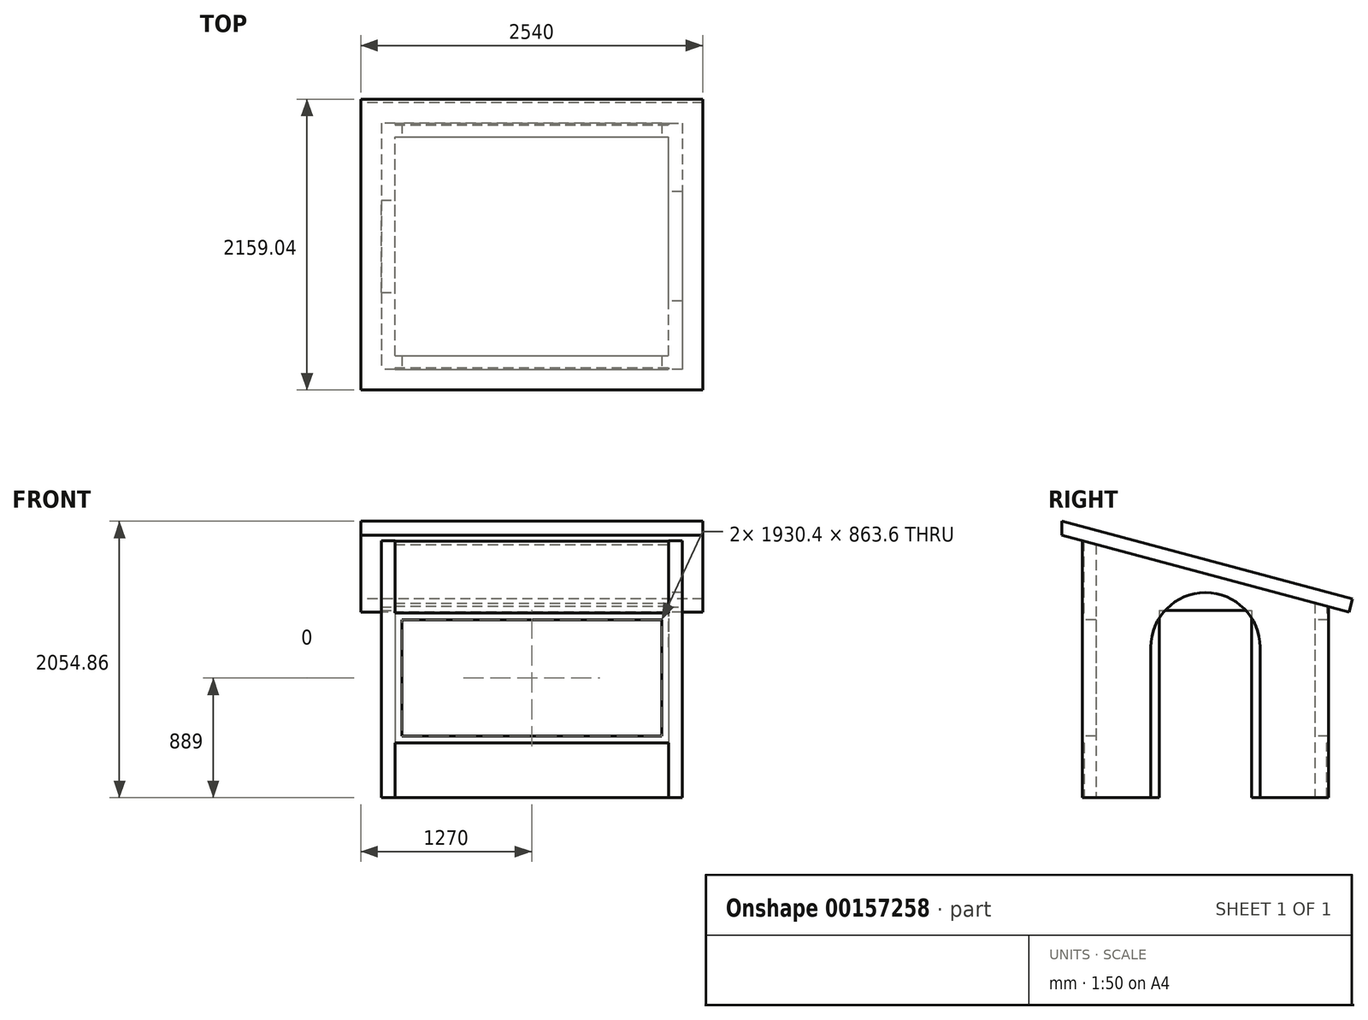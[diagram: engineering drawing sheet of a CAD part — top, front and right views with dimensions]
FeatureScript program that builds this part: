
annotation { "Feature Type Name" : "Feature", "Feature Type Description" : "" }
export const myFeature = defineFeature(function(context is Context, id is Id, definition is map)
    precondition{}
    {
        {
            var Q0;
            Q0=qCreatedBy(makeId("Right.planeOp"),FACE);
            var sketch = newSketch(context, id + "F0", { "sketchPlane" : qUnion([Q0])});
            skLineSegment(sketch, "E0", {"start": v(-914.4, 0) * mm, "end": v(-914.4, 2014.03) * mm});
            skLineSegment(sketch, "E1", {"start": v(-914.4, 2014.03) * mm, "end": v(914.4, 1524) * mm});
            skLineSegment(sketch, "E2", {"start": v(914.4, 1524) * mm, "end": v(914.4, 0) * mm});
            skLineSegment(sketch, "E3", {"start": v(914.4, 0) * mm, "end": v(-914.4, 0) * mm});
            skLineSegment(sketch, "E4", {"start": v(914.4, 1524) * mm, "end": v(-914.4, 1524) * mm, "construction": true});
            skLineSegment(sketch, "E5", {"start": v(0, 1524) * mm, "end": v(0, 0) * mm, "construction": true});
            skSolve(sketch);
        }
        {
            var Q0;
            Q0=makeQuery(id+"F0.imprint","IMPRINT",FACE,{"disambiguationData":[TD([[makeQuery(id+"F0.imprint","IMPRINT",EDGE,{"derivedFrom":sQuery(id+"F0.wireOp",EDGE,"E0")}),-1.0]])]});
            extrude(context, id + "F1", {"entities" : qUnion([Q0]), "endBound" : BoundingType.SYMMETRIC, "depth" : 2235.2 * mm});
        }
        {
            var Q0;
            Q0=qCreatedBy(makeId("Front.planeOp"),FACE);
            var sketch = newSketch(context, id + "F2", { "sketchPlane" : qUnion([Q0])});
            skLineSegment(sketch, "E6.bottom", {"start": v(-965.2, 1320.8) * mm, "end": v(965.2, 1320.8) * mm});
            skLineSegment(sketch, "E6.top", {"start": v(-965.2, 457.2) * mm, "end": v(965.2, 457.2) * mm});
            skLineSegment(sketch, "E6.left", {"start": v(-965.2, 1320.8) * mm, "end": v(-965.2, 457.2) * mm});
            skLineSegment(sketch, "E6.right", {"start": v(965.2, 1320.8) * mm, "end": v(965.2, 457.2) * mm});
            skLineSegment(sketch, "E7", {"start": v(0, 0) * mm, "end": v(0, 1954.27) * mm, "construction": true});
            skSolve(sketch);
        }
        {
            var Q0;
            Q0 = qSketchRegion(id + "F2", true);
            extrude(context, id + "F3", {"entities" : qUnion([Q0]), "operationType" : NewBodyOperationType.REMOVE, "endBound" : BoundingType.THROUGH_ALL, "oppositeDirection" : true, "depth" : 25.4 * mm, "hasSecondDirection" : true, "secondDirectionBound" : SecondDirectionBoundingType.THROUGH_ALL, "secondDirectionOppositeDirection" : false, "secondDirectionDepth" : 25.4 * mm});
        }
        {
            var Q0;
            Q0=qCreatedBy(makeId("Right.planeOp"),FACE);
            var sketch = newSketch(context, id + "F4", { "sketchPlane" : qUnion([Q0])});
            skLineSegment(sketch, "E8", {"start": v(0, 0) * mm, "end": v(0, 2189.15) * mm, "construction": true});
            skLineSegment(sketch, "E9.bottom", {"start": v(-342.9, 1390.65) * mm, "end": v(342.9, 1390.65) * mm});
            skLineSegment(sketch, "E9.top", {"start": v(-342.9, 0) * mm, "end": v(342.9, 0) * mm});
            skLineSegment(sketch, "E9.left", {"start": v(-342.9, 1390.65) * mm, "end": v(-342.9, 0) * mm});
            skLineSegment(sketch, "E9.right", {"start": v(342.9, 1390.65) * mm, "end": v(342.9, 0) * mm});
            skSolve(sketch);
        }
        {
            var Q0;
            Q0 = qSketchRegion(id + "F4", true);
            extrude(context, id + "F5", {"entities" : qUnion([Q0]), "operationType" : NewBodyOperationType.REMOVE, "endBound" : BoundingType.THROUGH_ALL, "oppositeDirection" : true, "depth" : 25.4 * mm});
        }
        {
            var Q0;
            Q0=qCreatedBy(makeId("Right.planeOp"),FACE);
            var sketch = newSketch(context, id + "F6", { "sketchPlane" : qUnion([Q0])});
            skLineSegment(sketch, "E10", {"start": v(-1066.8, 2054.86) * mm, "end": v(1092.24, 1476.35) * mm});
            skLineSegment(sketch, "E11", {"start": v(-1066.8, 2054.86) * mm, "end": v(-1066.8, 1949.68) * mm});
            skLineSegment(sketch, "E12", {"start": v(-1066.8, 1949.68) * mm, "end": v(1065.94, 1378.21) * mm});
            skLineSegment(sketch, "E13", {"start": v(1065.94, 1378.21) * mm, "end": v(1092.24, 1476.35) * mm});
            skSolve(sketch);
        }
        {
            var Q0;
            Q0=makeQuery(id+"F6.imprint","IMPRINT",FACE,{"disambiguationData":[TD([[makeQuery(id+"F6.imprint","IMPRINT",EDGE,{"derivedFrom":sQuery(id+"F6.wireOp",EDGE,"E10")}),-1.0]])]});
            extrude(context, id + "F7", {"entities" : qUnion([Q0]), "operationType" : NewBodyOperationType.ADD, "endBound" : BoundingType.SYMMETRIC, "depth" : 2540 * mm});
        }
        {
            var Q0;
            Q0=qCreatedBy(makeId("Top.planeOp"),FACE);
            var sketch = newSketch(context, id + "F8", { "sketchPlane" : qUnion([Q0])});
            skLineSegment(sketch, "E14", {"start": v(0, -730.46) * mm, "end": v(0, 588.36) * mm, "construction": true});
            skLineSegment(sketch, "E15", {"start": v(-1194.95, 0) * mm, "end": v(1199.4, 0) * mm, "construction": true});
            skLineSegment(sketch, "E16.bottom", {"start": v(-1016, -812.8) * mm, "end": v(1016, -812.8) * mm});
            skLineSegment(sketch, "E16.top", {"start": v(-1016, 812.8) * mm, "end": v(1016, 812.8) * mm});
            skLineSegment(sketch, "E16.left", {"start": v(-1016, -812.8) * mm, "end": v(-1016, 812.8) * mm});
            skLineSegment(sketch, "E16.right", {"start": v(1016, -812.8) * mm, "end": v(1016, 812.8) * mm});
            skSolve(sketch);
        }
        {
            var Q0;
            Q0 = qSketchRegion(id + "F8", true);
            var Q1;
            Q1=makeQuery(id+"F7.opExtrude","SWEPT_FACE",FACE,{"disambiguationData":[OSD([sQuery(id+"F6.wireOp",EDGE,"E12")])]});
            extrude(context, id + "F9", {"entities" : qUnion([Q0]), "operationType" : NewBodyOperationType.REMOVE, "endBound" : BoundingType.UP_TO_SURFACE, "endBoundEntityFace" : qUnion([Q1]), "depth" : 25.4 * mm});
        }
        {
            var Q0;
            Q0=qCreatedBy(makeId("Right.planeOp"),FACE);
            var sketch = newSketch(context, id + "F10", { "sketchPlane" : qUnion([Q0])});
            skLineSegment(sketch, "E17", {"start": v(0, 0) * mm, "end": v(0, 2220.14) * mm, "construction": true});
            skLineSegment(sketch, "E18", {"start": v(-406.4, 1117.6) * mm, "end": v(-406.4, 0) * mm});
            skLineSegment(sketch, "E19", {"start": v(-406.4, 0) * mm, "end": v(406.4, 0) * mm});
            skLineSegment(sketch, "E20", {"start": v(406.4, 0) * mm, "end": v(406.4, 1117.6) * mm});
            skArc(sketch, "E21", {"start": v(406.4, 1117.6) * mm, "mid": v(0, 1524) * mm, "end": v(-406.4, 1117.6) * mm});
            skSolve(sketch);
        }
        {
            var Q0;
            Q0 = qSketchRegion(id + "F10", true);
            extrude(context, id + "F11", {"entities" : qUnion([Q0]), "operationType" : NewBodyOperationType.REMOVE, "endBound" : BoundingType.THROUGH_ALL, "depth" : 25.4 * mm});
        }
        {
            var Q0;
            Q0=qCreatedBy(makeId("Right.planeOp"),FACE);
            var sketch = newSketch(context, id + "F12", { "sketchPlane" : qUnion([Q0])});
            skLineSegment(sketch, "E22.bottom", {"start": v(-901.7, 406.4) * mm, "end": v(-914.4, 406.4) * mm});
            skLineSegment(sketch, "E22.top", {"start": v(-901.7, 0) * mm, "end": v(-914.4, 0) * mm});
            skLineSegment(sketch, "E22.left", {"start": v(-901.7, 406.4) * mm, "end": v(-901.7, 0) * mm});
            skLineSegment(sketch, "E22.right", {"start": v(-914.4, 406.4) * mm, "end": v(-914.4, 0) * mm});
            skLineSegment(sketch, "E23.bottom", {"start": v(914.4, 0) * mm, "end": v(901.7, 0) * mm});
            skLineSegment(sketch, "E23.top", {"start": v(914.4, 406.4) * mm, "end": v(901.7, 406.4) * mm});
            skLineSegment(sketch, "E23.left", {"start": v(914.4, 0) * mm, "end": v(914.4, 406.4) * mm});
            skLineSegment(sketch, "E23.right", {"start": v(901.7, 0) * mm, "end": v(901.7, 406.4) * mm});
            skLineSegment(sketch, "E24", {"start": v(-914.4, 1908.84) * mm, "end": v(-914.4, 1371.6) * mm});
            skLineSegment(sketch, "E25", {"start": v(-914.4, 1371.6) * mm, "end": v(-901.7, 1371.6) * mm});
            skLineSegment(sketch, "E26", {"start": v(-901.7, 1371.6) * mm, "end": v(-901.7, 1905.44) * mm});
            skLineSegment(sketch, "E27", {"start": v(-901.7, 1905.44) * mm, "end": v(-914.4, 1908.84) * mm});
            skLineSegment(sketch, "E28", {"start": v(914.4, 1418.82) * mm, "end": v(901.7, 1422.22) * mm});
            skLineSegment(sketch, "E29", {"start": v(901.7, 1422.22) * mm, "end": v(901.7, 1371.6) * mm});
            skLineSegment(sketch, "E30", {"start": v(901.7, 1371.6) * mm, "end": v(914.4, 1371.6) * mm});
            skLineSegment(sketch, "E31", {"start": v(914.4, 1371.6) * mm, "end": v(914.4, 1418.82) * mm});
            skLineSegment(sketch, "E32", {"start": v(-914.4, 1371.6) * mm, "end": v(-914.4, 1908.84) * mm});
            skSolve(sketch);
        }
        {
            var Q0;
            Q0 = qSketchRegion(id + "F12", true);
            extrude(context, id + "F13", {"entities" : qUnion([Q0]), "operationType" : NewBodyOperationType.REMOVE, "endBound" : BoundingType.SYMMETRIC, "oppositeDirection" : true, "depth" : 2032 * mm});
        }
    });
